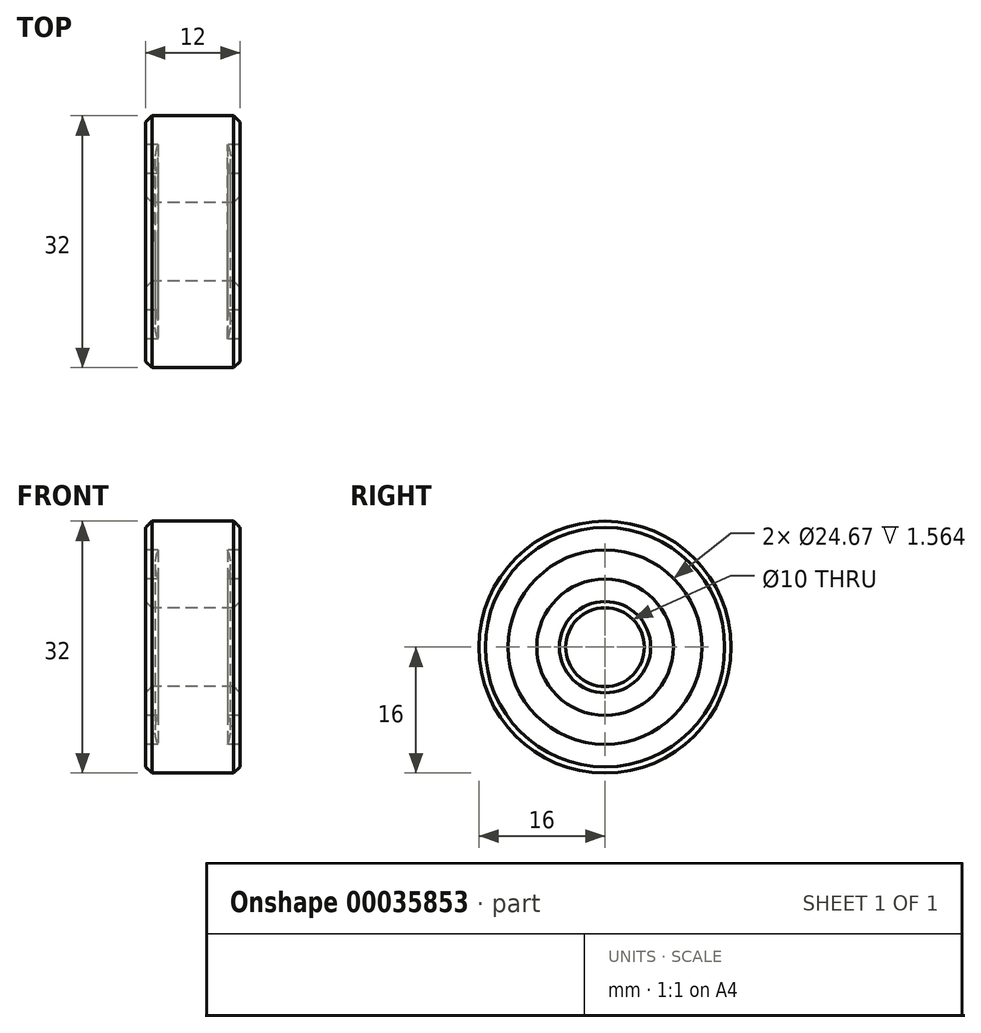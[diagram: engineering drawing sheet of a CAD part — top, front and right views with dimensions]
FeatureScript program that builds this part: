
annotation { "Feature Type Name" : "Feature", "Feature Type Description" : "" }
export const myFeature = defineFeature(function(context is Context, id is Id, definition is map)
    precondition{}
    {
        {
            assignVariable(context, id + "F0", {"name" : "W", "anyValue" : 12});
        }
        {
            var Q0;
            Q0=qCreatedBy(makeId("Front.planeOp"),FACE);
            var sketch = newSketch(context, id + "F1", { "sketchPlane" : qUnion([Q0])});
            skLineSegment(sketch, "E0.rect.bottom", {"start": v(6, 12.33) * mm, "end": v(4.44, 12.33) * mm});
            skLineSegment(sketch, "E0.rect.top", {"start": v(6, 16) * mm, "end": v(-6, 16) * mm});
            skLineSegment(sketch, "E0.rect.left", {"start": v(6, 12.33) * mm, "end": v(6, 16) * mm});
            skLineSegment(sketch, "E0.rect.right", {"start": v(-6, 12.33) * mm, "end": v(-6, 16) * mm});
            skPoint(sketch, "E0.rect.middle", {"position": v(0, 14.17) * mm});
            skLineSegment(sketch, "E1.rect.bottom", {"start": v(-6, 8.67) * mm, "end": v(-4.44, 8.67) * mm});
            skLineSegment(sketch, "E1.rect.top", {"start": v(-6, 5) * mm, "end": v(6, 5) * mm});
            skLineSegment(sketch, "E1.rect.left", {"start": v(-6, 8.67) * mm, "end": v(-6, 5) * mm});
            skLineSegment(sketch, "E1.rect.right", {"start": v(6, 8.67) * mm, "end": v(6, 5) * mm});
            skPoint(sketch, "E1.rect.middle", {"position": v(0, 6.83) * mm});
            skLineSegment(sketch, "E2", {"start": v(0, 12.33) * mm, "end": v(0, 8.67) * mm, "construction": true});
            skLineSegment(sketch, "E3", {"start": v(0, 10.5) * mm, "end": v(2, 10.5) * mm, "construction": true});
            skArc(sketch, "E4", {"start": v(-4.44, 12.33) * mm, "mid": v(-4.8, 10.5) * mm, "end": v(-4.44, 8.67) * mm});
            skLineSegment(sketch, "E5.trimOffspring", {"start": v(-4.44, 12.33) * mm, "end": v(-6, 12.33) * mm});
            skLineSegment(sketch, "E6.trimOffspring", {"start": v(4.44, 8.67) * mm, "end": v(6, 8.67) * mm});
            skArc(sketch, "E7.trimOffspring", {"start": v(4.44, 8.67) * mm, "mid": v(4.8, 10.5) * mm, "end": v(4.44, 12.33) * mm});
            skLineSegment(sketch, "E8", {"start": v(0, 0) * mm, "end": v(37.66, 0) * mm, "construction": true});
            skSolve(sketch);
        }
        {
            var Q0;
            Q0=makeQuery(id+"F1.imprint","IMPRINT",FACE,{"disambiguationData":[TD([[makeQuery(id+"F1.imprint","IMPRINT",EDGE,{"derivedFrom":sQuery(id+"F1.wireOp",EDGE,"E0.rect.bottom")}),-1.0]])]});
            var Q1;
            Q1=sQuery(id+"F1.wireOp",EDGE,"E8");
            revolve(context, id + "F2", {"entities" : qUnion([Q0]), "axis" : qUnion([Q1]), "revolveType" : RevolveType.FULL});
        }
        {
            var Q0;
            Q0=makeQuery(id+"F2.opRevolve","SWEPT_EDGE",EDGE,{"disambiguationData":[OSD([sQuery(id+"F1.wireOp",EDGE,"E0.rect.top"),sQuery(id+"F1.wireOp",EDGE,"E0.rect.right")])]});
            var Q1;
            Q1=makeQuery(id+"F2.opRevolve","SWEPT_EDGE",EDGE,{"disambiguationData":[OSD([sQuery(id+"F1.wireOp",EDGE,"E0.rect.top"),sQuery(id+"F1.wireOp",EDGE,"E0.rect.left")])]});
            var Q2;
            Q2=makeQuery(id+"F2.opRevolve","SWEPT_EDGE",EDGE,{"disambiguationData":[OSD([sQuery(id+"F1.wireOp",EDGE,"E1.rect.top"),sQuery(id+"F1.wireOp",EDGE,"E1.rect.right")])]});
            var Q3;
            Q3=makeQuery(id+"F2.opRevolve","SWEPT_EDGE",EDGE,{"disambiguationData":[OSD([sQuery(id+"F1.wireOp",EDGE,"E1.rect.top"),sQuery(id+"F1.wireOp",EDGE,"E1.rect.left")])]});
            chamfer(context, id + "F3", {"entities" : qUnion([Q0, Q1, Q2, Q3]), "width" : (getVariable(context, 'W') / 15) * mm, "tangentPropagation" : true});
        }
    });
